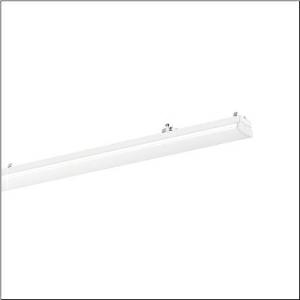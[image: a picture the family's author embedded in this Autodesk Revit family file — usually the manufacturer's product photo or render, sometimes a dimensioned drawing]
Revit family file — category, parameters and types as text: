
# Revit family: licross_11_recessed_opal_mo_51tl1ddv44xg
name_source: partatom
category: Lighting Fixtures
units: mm (PartAtom-declared; Revit-internal decimal feet)

## family parameters
Cut with Voids When Loaded = No
Host = Face
Light Source = No
Part Type = Normal
Room Calculation Point = No
Round Connector Dimension = Use Diameter
Shared = No

## types (1)
- --- (1 x LED, 4120 lm, 22.3 W, 4000K)
    Apparent Load = 22 VA
    CIE Flux Codes = 44 73 91 87 100
    Color Rendering = 80
    Color Temperature = 4000K
    Default Elevation = 1800 mm
    Description = Licross 11 recessed opal MO, luminaire insert, of sheet steel, coil coated, white, length: 2.250mm, width: 76mm, height: 87mm, LED rated luminous flux: 4.120lm, light colour: 840, SDCM (Standard Deviation of Colour Matching)MacAdam ≤ 2 SDCM (initial), control gear: DALI 2, with plug, 5-pole, with phase selection, mains connection: 220..240V, AC, 50/60Hz, rated input power: 22W, internal wiring halogen-free, primary optical cover: cover, of PMMA, light emission: direct with ceiling illumination distribution, primary light characteristic: symmetric, protection rating (complete): IP40, insulation class (complete): insulation class I (protective earthing), certification: CE, ENEC, VDE, UKCA, protection symbol: D if used in an environment without relevant dust loads with corresponding accessories, impact resistance: IK06, permissible ambient temperature for indoor applications: -25..+45°C, corresponds to IFS (International Featured Standards) requirements for safety and quality in the food industry, reducing of maximum allowable ambient temperature of 5°C with ceiling mounting, LABS conformity tested according to VDMA 24364:2018-05, The light source and the operating device comply with the requirements of the Ecodesign Regulation (EU) 2019/2020 and are replaceable in accordance with this regulation, packaging unit: 1 piece
    Height = 83 mm
    Lamp = 1 x LED
    Lamp Light Flux = 4120 lm
    Lamp Power = 22.3 W
    Lamp count = 1
    Length = 2250 mm
    Luminous efficacy = 185 lm/W
    Manufacturer = Siteco
    ModVariant = No
    Model = 51TL1DDV44XG
    Mounting Place = Ceiling
    Mounting Type = Pendant
    Number of Poles = 1
    OnlyDefault = Yes
    Power Factor = 1
    Product Name = Licross 11 recessed opal MO
    Product group = luminaire insert | ceiling pendant
    ProductGroupID = 901
    Protection Class = Protection class I
    Protection Degree = IP 40
    RLX_Detail_Level = 1
    RLX_Emergency_Light_Flux = 0 lm
    RLX_Emergency_Type = 0
    RLX_Emergency_Type_DB = No
    RlxData = <blob elided: 26485 chars, md5=5a4ff6f2>
    Socket = socket
    Standby Power = 0 W
    System Light Flux = 4120 lm
    System Power = 22 W
    Type Comments = factory setting: luminous flux: 100 % | dim-lin: 254 | 100 mA
    Type Image = l_1313666.jpg
    URL = http://relux.com
    VarID = @adj_084293
    Voltage = 0 V
    Weight = 0.00 kg
    Width = 76 mm

## geometry (parser evidence)
native form markers: Blend x4, Sweep x13
no freeform markers — native parametric forms only
